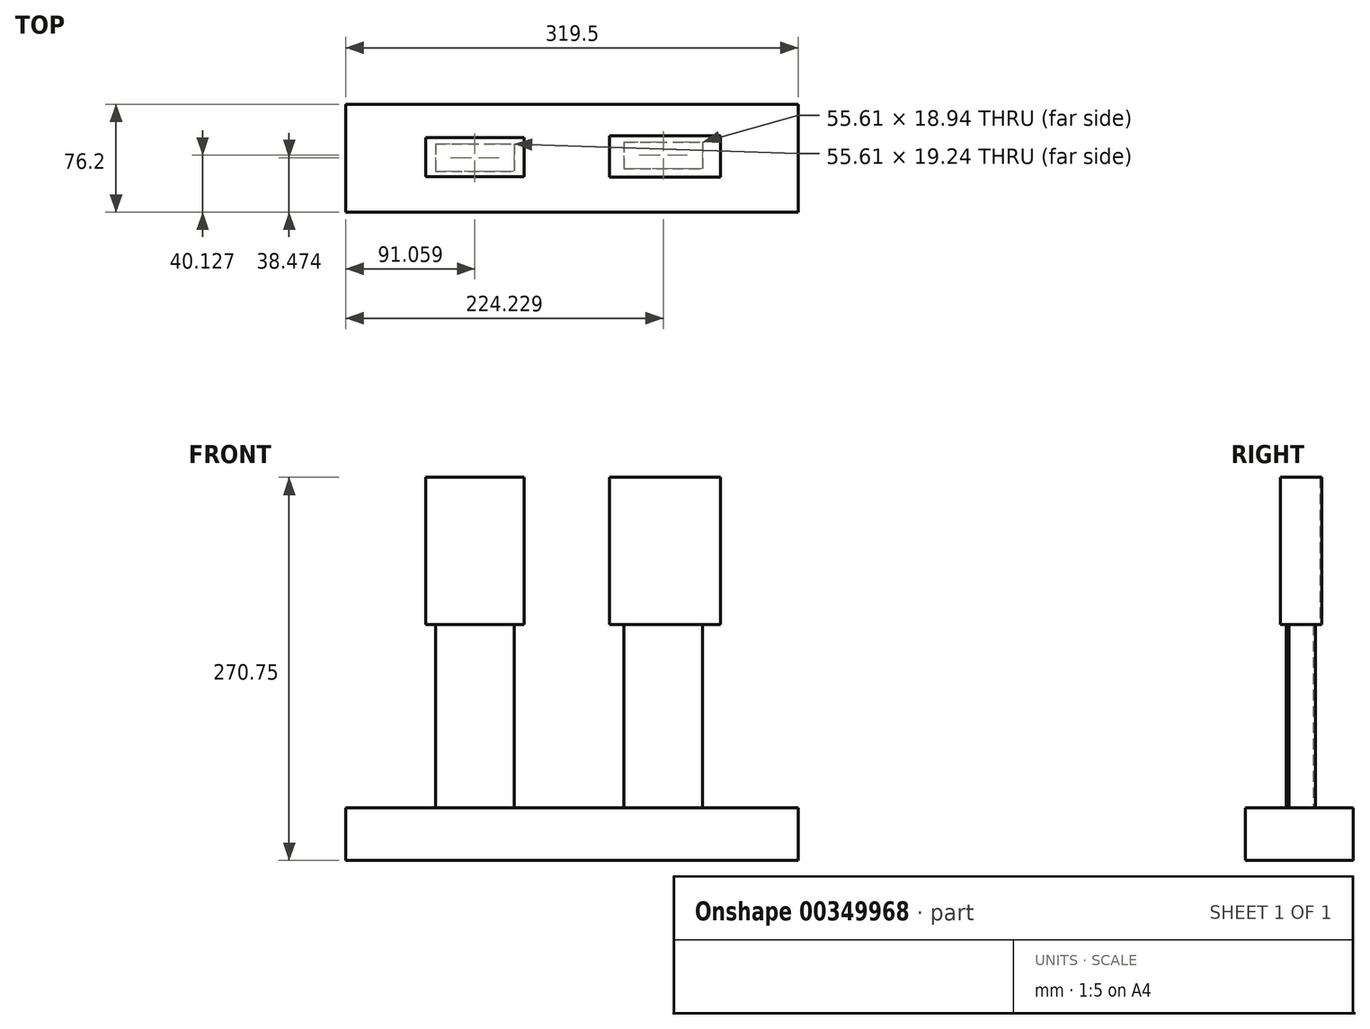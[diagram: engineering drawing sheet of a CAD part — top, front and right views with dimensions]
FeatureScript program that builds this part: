
annotation { "Feature Type Name" : "Feature", "Feature Type Description" : "" }
export const myFeature = defineFeature(function(context is Context, id is Id, definition is map)
    precondition{}
    {
        {
            var Q0;
            Q0=qCreatedBy(makeId("Front.planeOp"),FACE);
            var sketch = newSketch(context, id + "F0", { "sketchPlane" : qUnion([Q0])});
            skLineSegment(sketch, "E0.bottom", {"start": v(-126.06, -16.37) * mm, "end": v(193.44, -16.37) * mm});
            skLineSegment(sketch, "E0.top", {"start": v(-126.06, -53.44) * mm, "end": v(193.44, -53.44) * mm});
            skLineSegment(sketch, "E0.left", {"start": v(-126.06, -16.37) * mm, "end": v(-126.06, -53.44) * mm});
            skLineSegment(sketch, "E0.right", {"start": v(193.44, -16.37) * mm, "end": v(193.44, -53.44) * mm});
            skSolve(sketch);
        }
        {
            var Q0;
            Q0 = qSketchRegion(id + "F0", true);
            extrude(context, id + "F1", {"entities" : qUnion([Q0]), "depth" : 76.2 * mm});
        }
        {
            var Q0;
            Q0=makeQuery(id+"F1.opExtrude","SWEPT_FACE",FACE,{"disambiguationData":[OSD([sQuery(id+"F0.wireOp",EDGE,"E0.bottom")])]});
            var sketch = newSketch(context, id + "F2", { "sketchPlane" : qUnion([Q0])});
            skLineSegment(sketch, "E1.bottom", {"start": v(-62.8, -28.1) * mm, "end": v(-7.2, -28.1) * mm});
            skLineSegment(sketch, "E1.top", {"start": v(-62.8, -47.35) * mm, "end": v(-7.2, -47.35) * mm});
            skLineSegment(sketch, "E1.left", {"start": v(-62.8, -28.1) * mm, "end": v(-62.8, -47.35) * mm});
            skLineSegment(sketch, "E1.right", {"start": v(-7.2, -28.1) * mm, "end": v(-7.2, -47.35) * mm});
            skLineSegment(sketch, "E2.bottom", {"start": v(70.36, -26.6) * mm, "end": v(125.98, -26.6) * mm});
            skLineSegment(sketch, "E2.top", {"start": v(70.36, -45.54) * mm, "end": v(125.98, -45.54) * mm});
            skLineSegment(sketch, "E2.left", {"start": v(70.36, -26.6) * mm, "end": v(70.36, -45.54) * mm});
            skLineSegment(sketch, "E2.right", {"start": v(125.98, -26.6) * mm, "end": v(125.98, -45.54) * mm});
            skSolve(sketch);
        }
        {
            var Q0;
            Q0 = qSketchRegion(id + "F2", true);
            extrude(context, id + "F3", {"entities" : qUnion([Q0]), "operationType" : NewBodyOperationType.ADD, "depth" : 129.54 * mm});
        }
        {
            var Q0;
            Q0=makeQuery(id+"F3.opExtrude","CAP_FACE",FACE,{"disambiguationData":[OSD([sQuery(id+"F2.wireOp",EDGE,"E1.bottom"),sQuery(id+"F2.wireOp",EDGE,"E1.top"),sQuery(id+"F2.wireOp",EDGE,"E1.left"),sQuery(id+"F2.wireOp",EDGE,"E1.right")])],"isStart":false});
            var sketch = newSketch(context, id + "F4", { "sketchPlane" : qUnion([Q0])});
            skLineSegment(sketch, "E3.bottom", {"start": v(-69.77, -23.48) * mm, "end": v(0, -23.48) * mm});
            skLineSegment(sketch, "E3.top", {"start": v(-69.77, -51.1) * mm, "end": v(0, -51.1) * mm});
            skLineSegment(sketch, "E3.left", {"start": v(-69.77, -23.48) * mm, "end": v(-69.77, -51.1) * mm});
            skLineSegment(sketch, "E3.right", {"start": v(0, -23.48) * mm, "end": v(0, -51.1) * mm});
            skLineSegment(sketch, "E4.bottom", {"start": v(60.3, -22.22) * mm, "end": v(138.65, -22.22) * mm});
            skLineSegment(sketch, "E4.top", {"start": v(60.3, -51.35) * mm, "end": v(138.65, -51.35) * mm});
            skLineSegment(sketch, "E4.left", {"start": v(60.3, -22.22) * mm, "end": v(60.3, -51.35) * mm});
            skLineSegment(sketch, "E4.right", {"start": v(138.65, -22.22) * mm, "end": v(138.65, -51.35) * mm});
            skSolve(sketch);
        }
        {
            var Q0;
            Q0 = qSketchRegion(id + "F4", true);
            extrude(context, id + "F5", {"entities" : qUnion([Q0]), "operationType" : NewBodyOperationType.ADD, "depth" : 104.14 * mm});
        }
    });
